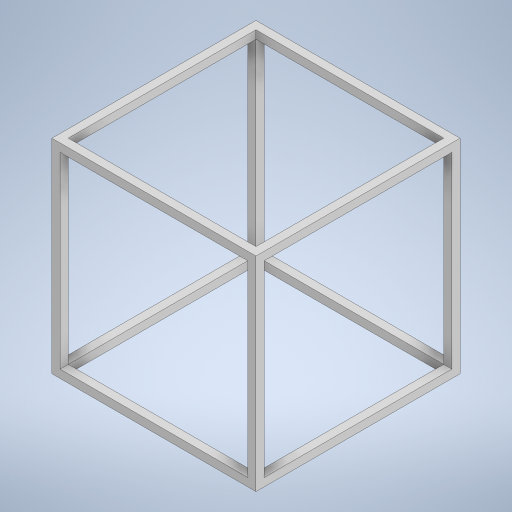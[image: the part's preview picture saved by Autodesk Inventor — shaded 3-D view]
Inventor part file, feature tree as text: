
AUTODESK INVENTOR PART (.ipt)
format: ipt  version: 2023.5 (Build 275446000, 446)  size: 291,328 bytes
history: native  units: mm
features: extrude x3, sketch x3, projected_geometry x2, other x1
ambient origin geometry x8: Origin, YZ Plane, XZ Plane, XY Plane, X Axis, Y Axis, Z Axis, Center Point
bodies: Body1 (feature_tree)
feature tree (9):
  other  "Bryła1"
  extrude  "Wyciągnięcie proste1"  Depth=50.0mm
  extrude  "Wyciągnięcie proste2"  Depth=50.0mm
  extrude  "Wyciągnięcie proste3"  Depth=2.0mm
  sketch  "Szkic1"
  sketch  "Szkic2"
  projected_geometry  "Pętla rzutowana1"
  sketch  "Szkic3"
  projected_geometry  "Pętla rzutowana2"
